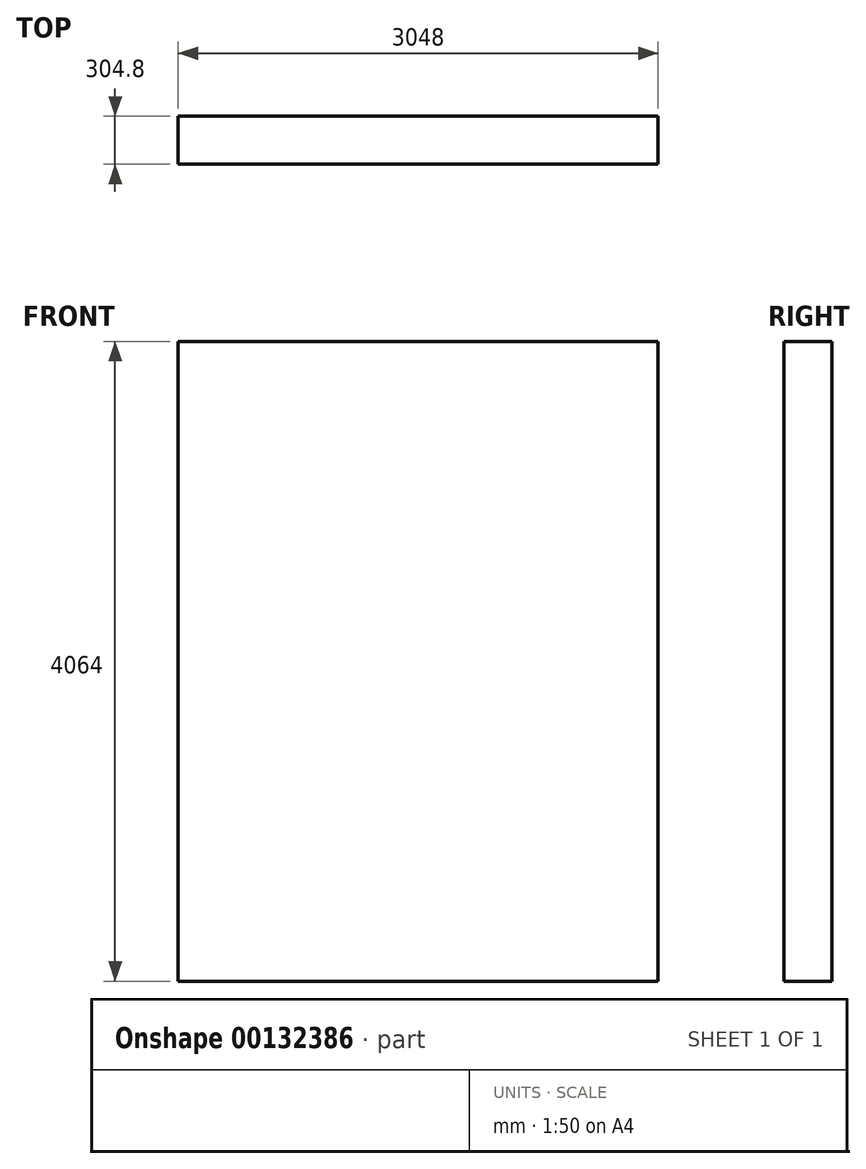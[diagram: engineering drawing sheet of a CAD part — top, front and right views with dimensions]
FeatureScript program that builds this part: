
annotation { "Feature Type Name" : "Feature", "Feature Type Description" : "" }
export const myFeature = defineFeature(function(context is Context, id is Id, definition is map)
    precondition{}
    {
        {
            var Q0;
            Q0=qCreatedBy(makeId("Front.planeOp"),FACE);
            var sketch = newSketch(context, id + "F0", { "sketchPlane" : qUnion([Q0])});
            skLineSegment(sketch, "E0.bottom", {"start": v(-1538.93, 2184.75) * mm, "end": v(1509.07, 2184.75) * mm});
            skLineSegment(sketch, "E0.top", {"start": v(-1538.93, -1879.25) * mm, "end": v(1509.07, -1879.25) * mm});
            skLineSegment(sketch, "E0.left", {"start": v(-1538.93, 2184.75) * mm, "end": v(-1538.93, -1879.25) * mm});
            skLineSegment(sketch, "E0.right", {"start": v(1509.07, 2184.75) * mm, "end": v(1509.07, -1879.25) * mm});
            skSolve(sketch);
        }
        {
            var Q0;
            Q0=makeQuery(id+"F0.imprint","IMPRINT",FACE,{"disambiguationData":[TD([[makeQuery(id+"F0.imprint","IMPRINT",EDGE,{"derivedFrom":sQuery(id+"F0.wireOp",EDGE,"E0.bottom")}),-1.0]])]});
            extrude(context, id + "F1", {"entities" : qUnion([Q0]), "depth" : 304.8 * mm});
        }
    });
